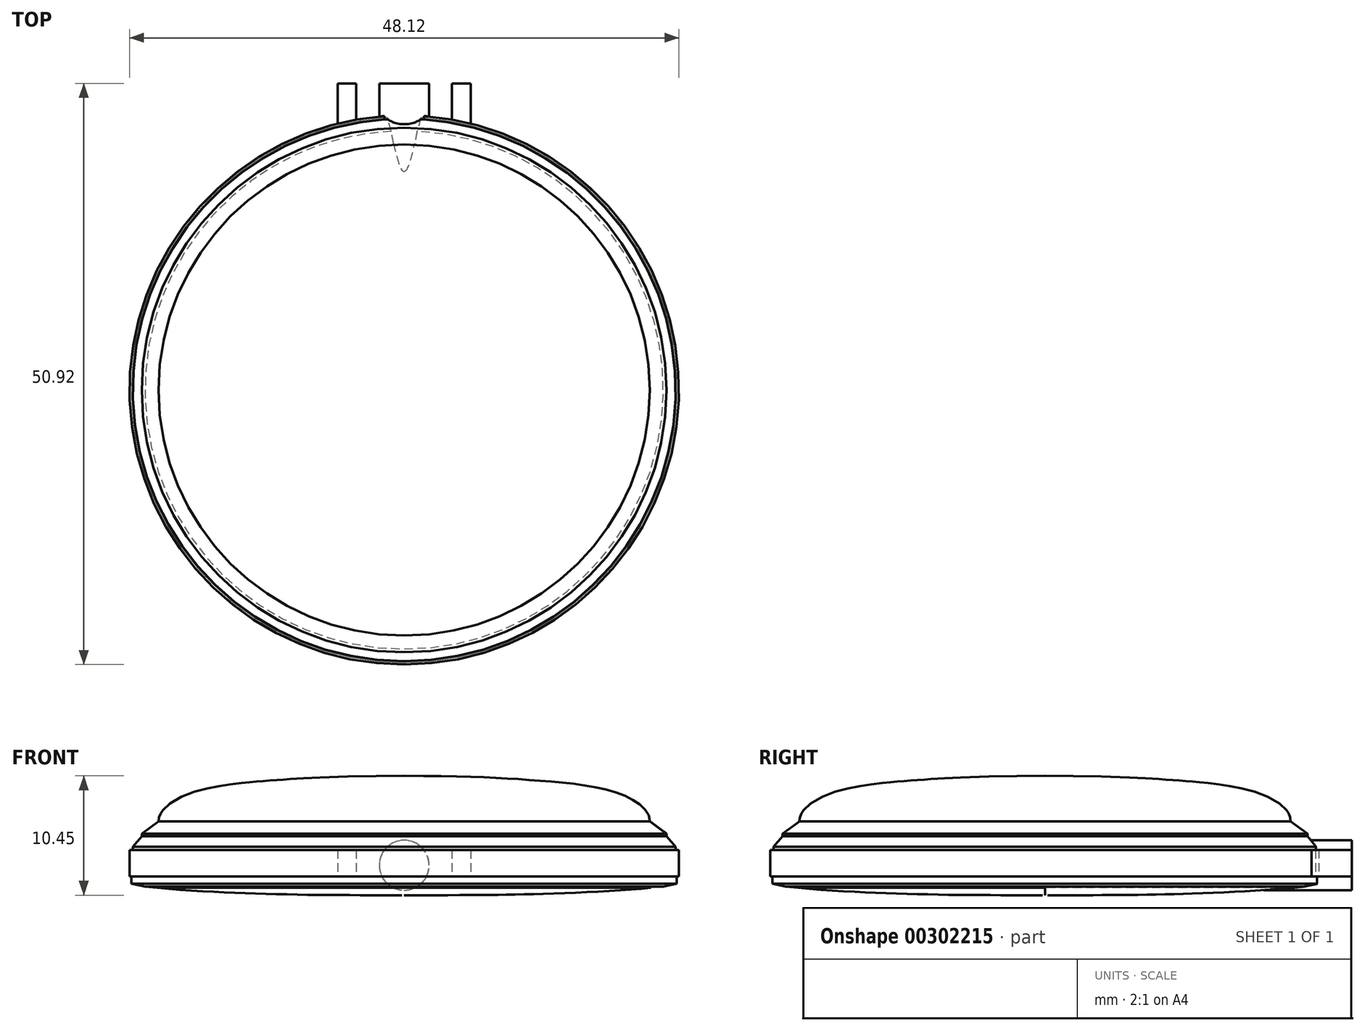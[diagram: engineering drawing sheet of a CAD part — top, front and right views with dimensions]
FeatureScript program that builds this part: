
annotation { "Feature Type Name" : "Feature", "Feature Type Description" : "" }
export const myFeature = defineFeature(function(context is Context, id is Id, definition is map)
    precondition{}
    {
        {
            var Q0;
            Q0=qCreatedBy(makeId("Top.planeOp"),FACE);
            var sketch = newSketch(context, id + "F0", { "sketchPlane" : qUnion([Q0])});
            skCircle(sketch, "E0", {"center": v(0, 0) * mm, "radius": 24.06 * mm});
            skSolve(sketch);
        }
        {
            var Q0;
            Q0=qSketchRegion(id+"F0",true);
            extrude(context, id + "F1", {"entities" : qUnion([Q0]), "depth" : 2.32 * mm});
        }
        {
            var Q0;
            Q0=qCreatedBy(makeId("Front.planeOp"),FACE);
            var sketch = newSketch(context, id + "F2", { "sketchPlane" : qUnion([Q0])});
            skLineSegment(sketch, "E1", {"start": v(0, 66.42) * mm, "end": v(0, -62.07) * mm, "construction": true});
            skFitSpline(sketch, "E2", {"points": [v(0, -1.65) * mm, v(10.95, -1.56) * mm, v(21.63, -1) * mm], "startDerivative": vector(34.83, 0) * mm, "endDerivative": vector(19.05, 1.97) * mm});
            skLineSegment(sketch, "E3", {"start": v(23.88, 0) * mm, "end": v(23.88, -0.66) * mm});
            skLineSegment(sketch, "E4", {"start": v(23.88, -0.66) * mm, "end": v(22.7, -0.9) * mm});
            skLineSegment(sketch, "E5", {"start": v(22.7, -0.9) * mm, "end": v(21.63, -1) * mm});
            skLineSegment(sketch, "E6", {"start": v(0, -1.65) * mm, "end": v(0, 0) * mm});
            skLineSegment(sketch, "E7", {"start": v(0, 0) * mm, "end": v(23.88, 0) * mm});
            skSolve(sketch);
        }
        {
            var Q0;
            Q0=qSketchRegion(id+"F2",true);
            var Q1;
            Q1=sQuery(id+"F2.wireOp",EDGE,"E1");
            revolve(context, id + "F3", {"operationType" : NewBodyOperationType.ADD, "entities" : qUnion([Q0]), "axis" : qUnion([Q1]), "revolveType" : RevolveType.FULL});
        }
        {
            var Q0;
            Q0=qCreatedBy(makeId("Front.planeOp"),FACE);
            var sketch = newSketch(context, id + "F4", { "sketchPlane" : qUnion([Q0])});
            skLineSegment(sketch, "E8", {"start": v(23.77, 2.32) * mm, "end": v(23.77, 2.6) * mm});
            skLineSegment(sketch, "E9", {"start": v(23.77, 2.6) * mm, "end": v(22.98, 3.5) * mm});
            skLineSegment(sketch, "E10", {"start": v(22.98, 3.5) * mm, "end": v(22.98, 3.74) * mm});
            skLineSegment(sketch, "E11", {"start": v(22.98, 3.74) * mm, "end": v(21.5, 4.82) * mm});
            skLineSegment(sketch, "E12", {"start": v(21.5, 4.82) * mm, "end": v(0, 4.82) * mm});
            skLineSegment(sketch, "E13", {"start": v(0, 4.82) * mm, "end": v(0, 2.32) * mm});
            skLineSegment(sketch, "E14", {"start": v(0, 2.32) * mm, "end": v(23.77, 2.32) * mm});
            skSolve(sketch);
        }
        {
            var Q0;
            Q0=qSketchRegion(id+"F4",true);
            var Q1;
            Q1=sQuery(id+"F2.wireOp",EDGE,"E1");
            revolve(context, id + "F5", {"operationType" : NewBodyOperationType.ADD, "entities" : qUnion([Q0]), "axis" : qUnion([Q1]), "revolveType" : RevolveType.FULL});
        }
        {
            var Q0;
            Q0=qCreatedBy(makeId("Front.planeOp"),FACE);
            var sketch = newSketch(context, id + "F6", { "sketchPlane" : qUnion([Q0])});
            skFitSpline(sketch, "E15", {"points": [v(21.51, 4.82) * mm, v(19.12, 7.14) * mm, v(11.78, 8.39) * mm, v(0, 8.8) * mm], "startDerivative": vector(0, 12.59) * mm, "endDerivative": vector(-41.08, 0) * mm});
            skLineSegment(sketch, "E16", {"start": v(0, 8.8) * mm, "end": v(0, 4.82) * mm});
            skLineSegment(sketch, "E17", {"start": v(0, 4.82) * mm, "end": v(21.51, 4.82) * mm});
            skSolve(sketch);
        }
        {
            var Q0;
            Q0=qSketchRegion(id+"F6",true);
            var Q1;
            Q1=sQuery(id+"F2.wireOp",EDGE,"E1");
            revolve(context, id + "F7", {"operationType" : NewBodyOperationType.ADD, "entities" : qUnion([Q0]), "axis" : qUnion([Q1]), "revolveType" : RevolveType.FULL});
        }
        {
            var Q0;
            Q0=qCreatedBy(makeId("Top.planeOp"),FACE);
            var sketch = newSketch(context, id + "F8", { "sketchPlane" : qUnion([Q0])});
            skLineSegment(sketch, "E18", {"start": v(0, 37.72) * mm, "end": v(0, 2.03) * mm, "construction": true});
            skLineSegment(sketch, "E19", {"start": v(4.2, 23.69) * mm, "end": v(4.2, 26.86) * mm});
            skLineSegment(sketch, "E20", {"start": v(4.2, 26.86) * mm, "end": v(5.82, 26.86) * mm});
            skLineSegment(sketch, "E21", {"start": v(5.82, 26.86) * mm, "end": v(5.82, 23.34) * mm});
            skLineSegment(sketch, "E22", {"start": v(5.82, 23.34) * mm, "end": v(4.96, 22.06) * mm});
            skLineSegment(sketch, "E23", {"start": v(4.96, 22.06) * mm, "end": v(4.2, 23.69) * mm});
            skLineSegment(sketch, "E24.MirrorCS", {"start": v(-5.82, 23.34) * mm, "end": v(-4.96, 22.06) * mm});
            skLineSegment(sketch, "E25.MirrorCS", {"start": v(-5.82, 26.86) * mm, "end": v(-5.82, 23.34) * mm});
            skLineSegment(sketch, "E26.MirrorCS", {"start": v(-4.96, 22.06) * mm, "end": v(-4.19, 23.69) * mm});
            skLineSegment(sketch, "E27.MirrorCS", {"start": v(-4.19, 23.69) * mm, "end": v(-4.19, 26.86) * mm});
            skLineSegment(sketch, "E28.MirrorCS", {"start": v(-4.19, 26.86) * mm, "end": v(-5.82, 26.86) * mm});
            skCircle(sketch, "E29.0.0", {"center": v(0, 0) * mm, "radius": 24.06 * mm, "construction": true});
            skSolve(sketch);
        }
        {
            var Q0;
            Q0=qSketchRegion(id+"F8",true);
            extrude(context, id + "F9", {"entities" : qUnion([Q0]), "operationType" : NewBodyOperationType.ADD, "depth" : 2.3 * mm});
        }
        {
            var Q0;
            Q0=qCreatedBy(makeId("Front.planeOp"),FACE);
            var sketch = newSketch(context, id + "F10", { "sketchPlane" : qUnion([Q0])});
            skLineSegment(sketch, "E30", {"start": v(0, 0) * mm, "end": v(0, 17.8) * mm, "construction": true});
            skCircle(sketch, "E31", {"center": v(0, 0.97) * mm, "radius": 2.19 * mm});
            skSolve(sketch);
        }
        {
            var Q0;
            Q0=qSketchRegion(id+"F10",true);
            extrude(context, id + "F11", {"entities" : qUnion([Q0]), "operationType" : NewBodyOperationType.ADD, "oppositeDirection" : true, "depth" : 26.86 * mm});
        }
    });
